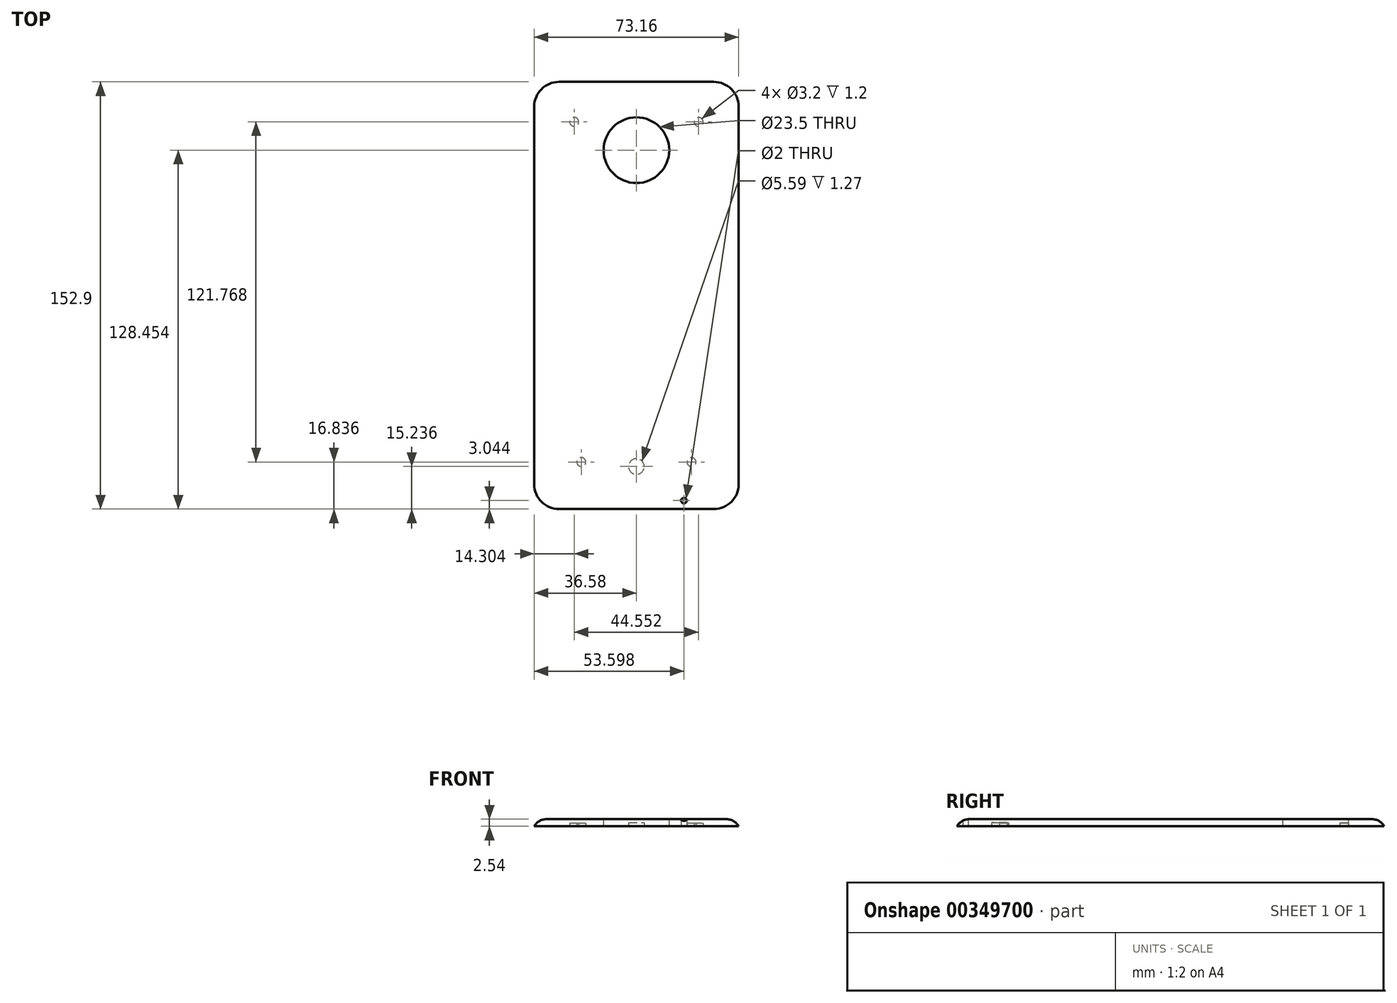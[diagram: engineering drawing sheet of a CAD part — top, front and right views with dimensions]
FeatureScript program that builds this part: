
annotation { "Feature Type Name" : "Feature", "Feature Type Description" : "" }
export const myFeature = defineFeature(function(context is Context, id is Id, definition is map)
    precondition{}
    {
        {
            var Q0;
            Q0=qCreatedBy(makeId("Top.planeOp"),FACE);
            var sketch = newSketch(context, id + "F0", { "sketchPlane" : qUnion([Q0])});
            skLineSegment(sketch, "E0", {"start": v(0, 76.45) * mm, "end": v(36.58, 76.45) * mm});
            skLineSegment(sketch, "E1", {"start": v(36.58, 76.45) * mm, "end": v(36.58, 0) * mm});
            skLineSegment(sketch, "E2.MirrorCS", {"start": v(36.58, -76.45) * mm, "end": v(36.58, 0) * mm});
            skLineSegment(sketch, "E3.MirrorCS", {"start": v(0, -76.45) * mm, "end": v(36.58, -76.45) * mm});
            skLineSegment(sketch, "E4.MirrorCS", {"start": v(-36.58, 76.45) * mm, "end": v(-36.58, 0) * mm});
            skLineSegment(sketch, "E5.MirrorCS", {"start": v(-36.58, -76.45) * mm, "end": v(-36.58, 0) * mm});
            skLineSegment(sketch, "E6.MirrorCS", {"start": v(0, -76.45) * mm, "end": v(-36.58, -76.45) * mm});
            skLineSegment(sketch, "E7.MirrorCS", {"start": v(0, 76.45) * mm, "end": v(-36.58, 76.45) * mm});
            skSolve(sketch);
        }
        {
            var Q0;
            Q0=makeQuery(id+"F0.imprint","IMPRINT",FACE,{"disambiguationData":[TD([[makeQuery(id+"F0.imprint","IMPRINT",EDGE,{"derivedFrom":sQuery(id+"F0.wireOp",EDGE,"E0")}),-1.0]])]});
            extrude(context, id + "F1", {"entities" : qUnion([Q0]), "depth" : 2.54 * mm});
        }
        {
            var Q0;
            Q0=makeQuery(id+"F1.opExtrude","CAP_FACE",FACE,{"disambiguationData":[OSD([sQuery(id+"F0.wireOp",EDGE,"E0"),sQuery(id+"F0.wireOp",EDGE,"E2.MirrorCS"),sQuery(id+"F0.wireOp",EDGE,"E3.MirrorCS"),sQuery(id+"F0.wireOp",EDGE,"E1"),sQuery(id+"F0.wireOp",EDGE,"E4.MirrorCS"),sQuery(id+"F0.wireOp",EDGE,"E6.MirrorCS"),sQuery(id+"F0.wireOp",EDGE,"E5.MirrorCS"),sQuery(id+"F0.wireOp",EDGE,"E7.MirrorCS")])],"isStart":false});
            var sketch = newSketch(context, id + "F2", { "sketchPlane" : qUnion([Q0])});
            skCircle(sketch, "E8", {"center": v(0, 52) * mm, "radius": 11.75 * mm});
            skSolve(sketch);
        }
        {
            var Q0;
            Q0 = qSketchRegion(id + "F2", true);
            extrude(context, id + "F3", {"entities" : qUnion([Q0]), "operationType" : NewBodyOperationType.REMOVE, "endBound" : BoundingType.THROUGH_ALL, "oppositeDirection" : true, "depth" : 25.4 * mm});
        }
        {
            var Q0;
            Q0=makeQuery(id+"F1.opExtrude","SWEPT_EDGE",EDGE,{"disambiguationData":[OSD([sQuery(id+"F0.wireOp",EDGE,"E4.MirrorCS"),sQuery(id+"F0.wireOp",EDGE,"E7.MirrorCS")])]});
            var Q1;
            Q1=makeQuery(id+"F1.opExtrude","SWEPT_EDGE",EDGE,{"disambiguationData":[OSD([sQuery(id+"F0.wireOp",EDGE,"E0"),sQuery(id+"F0.wireOp",EDGE,"E1")])]});
            var Q2;
            Q2=makeQuery(id+"F1.opExtrude","SWEPT_EDGE",EDGE,{"disambiguationData":[OSD([sQuery(id+"F0.wireOp",EDGE,"E2.MirrorCS"),sQuery(id+"F0.wireOp",EDGE,"E3.MirrorCS")])]});
            var Q3;
            Q3=makeQuery(id+"F1.opExtrude","SWEPT_EDGE",EDGE,{"disambiguationData":[OSD([sQuery(id+"F0.wireOp",EDGE,"E6.MirrorCS"),sQuery(id+"F0.wireOp",EDGE,"E5.MirrorCS")])]});
            fillet(context, id + "F4", {"entities" : qUnion([Q0, Q1, Q2, Q3]), "radius" : 8.9 * mm, "tangentPropagation" : true, "allowEdgeOverflow" : false});
        }
        {
            var Q0;
            Q0=makeQuery(id+"F1.opExtrude","CAP_EDGE",EDGE,{"disambiguationData":[OSD([sQuery(id+"F0.wireOp",EDGE,"E2.MirrorCS"),sQuery(id+"F0.wireOp",EDGE,"E1")])],"isStart":false});
            fillet(context, id + "F5", {"entities" : qUnion([Q0]), "radius" : 5.08 * mm, "tangentPropagation" : true, "allowEdgeOverflow" : false});
        }
        {
            var Q0;
            Q0=makeQuery(id+"F1.opExtrude","CAP_FACE",FACE,{"disambiguationData":[OSD([sQuery(id+"F0.wireOp",EDGE,"E0"),sQuery(id+"F0.wireOp",EDGE,"E2.MirrorCS"),sQuery(id+"F0.wireOp",EDGE,"E3.MirrorCS"),sQuery(id+"F0.wireOp",EDGE,"E1"),sQuery(id+"F0.wireOp",EDGE,"E4.MirrorCS"),sQuery(id+"F0.wireOp",EDGE,"E6.MirrorCS"),sQuery(id+"F0.wireOp",EDGE,"E5.MirrorCS"),sQuery(id+"F0.wireOp",EDGE,"E7.MirrorCS")])],"isStart":true});
            var sketch = newSketch(context, id + "F6", { "sketchPlane" : qUnion([Q0])});
            skCircle(sketch, "E9", {"center": v(17.02, 73.4) * mm, "radius": 1 * mm});
            skSolve(sketch);
        }
        {
            var Q0;
            Q0=makeQuery(id+"F6.imprint","IMPRINT",FACE,{"disambiguationData":[TD([[makeQuery(id+"F6.imprint","IMPRINT",EDGE,{"derivedFrom":sQuery(id+"F6.wireOp",EDGE,"E9")}),1.0]])]});
            extrude(context, id + "F7", {"entities" : qUnion([Q0]), "operationType" : NewBodyOperationType.REMOVE, "endBound" : BoundingType.THROUGH_ALL, "oppositeDirection" : true, "depth" : 25.4 * mm});
        }
        {
            var Q0;
            Q0=makeQuery(id+"F1.opExtrude","CAP_FACE",FACE,{"disambiguationData":[OSD([sQuery(id+"F0.wireOp",EDGE,"E0"),sQuery(id+"F0.wireOp",EDGE,"E2.MirrorCS"),sQuery(id+"F0.wireOp",EDGE,"E3.MirrorCS"),sQuery(id+"F0.wireOp",EDGE,"E1"),sQuery(id+"F0.wireOp",EDGE,"E4.MirrorCS"),sQuery(id+"F0.wireOp",EDGE,"E6.MirrorCS"),sQuery(id+"F0.wireOp",EDGE,"E5.MirrorCS"),sQuery(id+"F0.wireOp",EDGE,"E7.MirrorCS")])],"isStart":true});
            var sketch = newSketch(context, id + "F8", { "sketchPlane" : qUnion([Q0])});
            skCircle(sketch, "E10", {"center": v(-22.28, -62.15) * mm, "radius": 1.6 * mm});
            skCircle(sketch, "E11.MirrorC", {"center": v(22.28, -62.15) * mm, "radius": 1.6 * mm});
            skSolve(sketch);
        }
        {
            var Q0;
            Q0=makeQuery(id+"F1.opExtrude","CAP_FACE",FACE,{"disambiguationData":[OSD([sQuery(id+"F0.wireOp",EDGE,"E0"),sQuery(id+"F0.wireOp",EDGE,"E2.MirrorCS"),sQuery(id+"F0.wireOp",EDGE,"E3.MirrorCS"),sQuery(id+"F0.wireOp",EDGE,"E1"),sQuery(id+"F0.wireOp",EDGE,"E4.MirrorCS"),sQuery(id+"F0.wireOp",EDGE,"E6.MirrorCS"),sQuery(id+"F0.wireOp",EDGE,"E5.MirrorCS"),sQuery(id+"F0.wireOp",EDGE,"E7.MirrorCS")])],"isStart":true});
            var sketch = newSketch(context, id + "F9", { "sketchPlane" : qUnion([Q0])});
            skCircle(sketch, "E12", {"center": v(19.74, 59.61) * mm, "radius": 1.6 * mm});
            skCircle(sketch, "E13.MirrorC", {"center": v(-19.74, 59.61) * mm, "radius": 1.6 * mm});
            skLineSegment(sketch, "E14", {"start": v(19.74, 59.61) * mm, "end": v(-19.74, 59.61) * mm, "construction": true});
            skSolve(sketch);
        }
        {
            var Q0;
            Q0 = qSketchRegion(id + "F9", true);
            var Q1;
            Q1 = qSketchRegion(id + "F8", true);
            extrude(context, id + "F10", {"entities" : qUnion([Q0, Q1]), "operationType" : NewBodyOperationType.REMOVE, "oppositeDirection" : true, "depth" : 1.2 * mm});
        }
        {
            var Q0;
            Q0=makeQuery(id+"F1.opExtrude","CAP_FACE",FACE,{"disambiguationData":[OSD([sQuery(id+"F0.wireOp",EDGE,"E0"),sQuery(id+"F0.wireOp",EDGE,"E2.MirrorCS"),sQuery(id+"F0.wireOp",EDGE,"E3.MirrorCS"),sQuery(id+"F0.wireOp",EDGE,"E1"),sQuery(id+"F0.wireOp",EDGE,"E4.MirrorCS"),sQuery(id+"F0.wireOp",EDGE,"E6.MirrorCS"),sQuery(id+"F0.wireOp",EDGE,"E5.MirrorCS"),sQuery(id+"F0.wireOp",EDGE,"E7.MirrorCS")])],"isStart":true});
            var sketch = newSketch(context, id + "F11", { "sketchPlane" : qUnion([Q0])});
            skCircle(sketch, "E15", {"center": v(0, 61.21) * mm, "radius": 2.8 * mm});
            skSolve(sketch);
        }
        {
            var Q0;
            Q0 = qSketchRegion(id + "F11", true);
            extrude(context, id + "F12", {"entities" : qUnion([Q0]), "operationType" : NewBodyOperationType.REMOVE, "oppositeDirection" : true, "depth" : 1.27 * mm});
        }
    });
